# Revit family: 306_EP_R+BAC
name_source: partatom
category: Pipe Accessories
units: mm (PartAtom-declared; Revit-internal decimal feet)

## family parameters
Always vertical = Yes
Cut with Voids When Loaded = No
Part Type = Valve - Breaks Into
Round Connector Dimension = Use Diameter
Shared = No
Work Plane-Based = No

## types (6) — shared parameters
B1 = 13 mm
B11 = 38 mm
B2 = 19 mm  [stored 0.062336 ft]
CAT0 = Yes
DXX = 10 mm  [stored 0.0328084 ft]
Description = Characterised control valve (CCV), 2-way, Internal thread
L2D_Min = 3048 mm
L7 = 5 mm  [stored 0.0164042 ft]
LTT = 10 mm  [stored 0.0328084 ft]
LTT__ve = -10 mm  [stored -0.0328084 ft]
Manufacturer = Belimo
QmdConnectorList = 301;D;302;D
R55 = 9 mm  [stored 0.0295276 ft]
R9 = 18 mm  [stored 0.0590551 ft]
magiPartTypeId = 306
magiProductFamilyId = EP*R+BAC
zero-valued in all types: MC_Default_elevation

## per-type parameters (varying)
- EV015R+BAC: D=15 mm; D22=8 mm  [stored 0.0262467 ft]; DX2=15 mm  [stored 0.0492126 ft]; H=160 mm; L=192 mm; L1=16 mm; L11=8 mm  [stored 0.0262467 ft]; L2=81 mm; L2D=191 mm; L5=21 mm  [stored 0.0688976 ft]; L6=11 mm; L8=21 mm  [stored 0.0688976 ft]; LL=96 mm; LX=69 mm; R7=12 mm  [stored 0.0393701 ft]; RR=13 mm; W2D=15 mm  [stored 0.0492126 ft]; X2=83 mm; X22=47 mm; X22__ve=-47 mm; X3=41 mm; X4=19 mm  [stored 0.062336 ft]; X5=49 mm; XX1=60 mm; Z1=20 mm  [stored 0.0656168 ft]; Z4=22 mm; Z5=14 mm  [stored 0.0459318 ft]; Z54=22 mm; Z55=7 mm  [stored 0.0229659 ft]; Z6=26 mm  [stored 0.0853018 ft]; Z66=20 mm  [stored 0.0656168 ft]; ZX1=70 mm; ZX2=50 mm; ZX3=24 mm; ZX4=40 mm  [stored 0.131234 ft]
- EV050R+BAC: D=50 mm; D22=13 mm; DX2=25 mm  [stored 0.082021 ft]; H=177 mm; L=288 mm; L1=24 mm; L11=12 mm  [stored 0.0393701 ft]; L2=69 mm; L2D=284 mm; L5=31 mm; L6=19 mm  [stored 0.062336 ft]; L8=31 mm; LL=144 mm; LX=93 mm; R7=20 mm  [stored 0.0656168 ft]; RR=30 mm  [stored 0.0984252 ft]; W2D=50 mm; X2=107 mm; X22=71 mm; X22__ve=-71 mm; X3=59 mm; X4=50 mm; X5=71 mm; XX1=89 mm; Z1=22 mm; Z4=25 mm  [stored 0.082021 ft]; Z5=16 mm; Z54=25 mm  [stored 0.082021 ft]; Z55=8 mm  [stored 0.0262467 ft]; Z6=29 mm; Z66=22 mm; ZX1=77 mm; ZX2=55 mm; ZX3=27 mm; ZX4=44 mm
- EV040R+BAC: D=40 mm; D22=20 mm  [stored 0.0656168 ft]; DX2=40 mm  [stored 0.131234 ft]; H=172 mm; L=267 mm; L1=23 mm; L11=11 mm; L2=65 mm; L2D=274 mm; L5=29 mm; L6=18 mm  [stored 0.0590551 ft]; L8=29 mm; LL=134 mm; LX=88 mm; R7=32 mm; RR=25 mm  [stored 0.082021 ft]; W2D=40 mm  [stored 0.131234 ft]; X2=107 mm; X22=67 mm; X22__ve=-67 mm; X3=57 mm; X4=39 mm; X5=68 mm; XX1=84 mm; Z1=22 mm; Z4=24 mm; Z5=16 mm; Z54=24 mm; Z55=8 mm  [stored 0.0262467 ft]; Z6=28 mm; Z66=21 mm  [stored 0.0688976 ft]; ZX1=75 mm; ZX2=54 mm; ZX3=26 mm  [stored 0.0853018 ft]; ZX4=43 mm
- EV032R+BAC: D=32 mm; D22=16 mm; DX2=32 mm; H=168 mm; L=255 mm; L1=21 mm  [stored 0.0688976 ft]; L11=11 mm; L2=68 mm; L2D=254 mm; L5=27 mm; L6=16 mm; L8=27 mm; LL=128 mm; LX=87 mm; R7=26 mm  [stored 0.0853018 ft]; RR=21 mm  [stored 0.0688976 ft]; W2D=32 mm; X2=106 mm; X22=63 mm; X22__ve=-63 mm; X3=53 mm; X4=36 mm; X5=63 mm; XX1=79 mm; Z1=21 mm  [stored 0.0688976 ft]; Z4=23 mm; Z5=15 mm  [stored 0.0492126 ft]; Z54=23 mm; Z55=8 mm  [stored 0.0262467 ft]; Z6=28 mm; Z66=21 mm  [stored 0.0688976 ft]; ZX1=74 mm; ZX2=53 mm; ZX3=25 mm  [stored 0.082021 ft]; ZX4=42 mm
- EV025R+BAC: D=25 mm; D22=13 mm; DX2=25 mm  [stored 0.082021 ft]; H=165 mm; L=230 mm; L1=19 mm  [stored 0.062336 ft]; L11=10 mm  [stored 0.0328084 ft]; L2=71 mm; L2D=231 mm; L5=25 mm  [stored 0.082021 ft]; L6=14 mm  [stored 0.0459318 ft]; L8=25 mm  [stored 0.082021 ft]; LL=115 mm; LX=80 mm; R7=20 mm  [stored 0.0656168 ft]; RR=18 mm  [stored 0.0590551 ft]; W2D=25 mm  [stored 0.082021 ft]; X2=89 mm; X22=57 mm; X22__ve=-57 mm; X3=49 mm; X4=27 mm; X5=58 mm; XX1=72 mm; Z1=21 mm  [stored 0.0688976 ft]; Z4=23 mm; Z5=15 mm  [stored 0.0492126 ft]; Z54=23 mm; Z55=8 mm  [stored 0.0262467 ft]; Z6=27 mm; Z66=20 mm  [stored 0.0656168 ft]; ZX1=72 mm; ZX2=52 mm; ZX3=25 mm  [stored 0.082021 ft]; ZX4=41 mm
- EV020R+BAC: D=20 mm; D22=10 mm  [stored 0.0328084 ft]; DX2=20 mm  [stored 0.0656168 ft]; H=162 mm; L=211 mm; L1=18 mm  [stored 0.0590551 ft]; L11=9 mm  [stored 0.0295276 ft]; L2=75 mm; L2D=203 mm; L5=24 mm; L6=13 mm; L8=24 mm; LL=106 mm; LX=74 mm; R7=16 mm; RR=15 mm  [stored 0.0492126 ft]; W2D=20 mm  [stored 0.0656168 ft]; X2=95 mm; X22=53 mm; X22__ve=-53 mm; X3=45 mm; X4=22 mm; X5=54 mm; XX1=66 mm; Z1=20 mm  [stored 0.0656168 ft]; Z4=22 mm; Z5=15 mm  [stored 0.0492126 ft]; Z54=22 mm; Z55=7 mm  [stored 0.0229659 ft]; Z6=26 mm  [stored 0.0853018 ft]; Z66=20 mm  [stored 0.0656168 ft]; ZX1=71 mm; ZX2=51 mm; ZX3=24 mm; ZX4=41 mm

note: column(s) folded — value = type name in every type: magiProductCode, magiProductId

note: [stored X ft] marks values corroborated as IEEE doubles in the binary element streams (Revit-internal decimal feet)

## geometry (parser evidence)
native form markers: Sweep x3
no freeform markers — native parametric forms only
